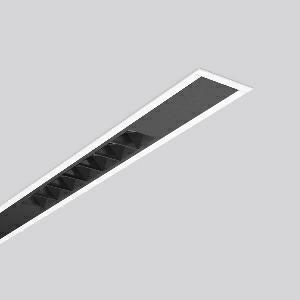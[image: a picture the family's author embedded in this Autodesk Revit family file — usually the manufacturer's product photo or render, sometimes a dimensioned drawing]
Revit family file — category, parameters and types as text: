
# Revit family: less_is_more_beamline_312481_002_1_76_a936
name_source: partatom
category: Lighting Fixtures
units: mm (PartAtom-declared; Revit-internal decimal feet)

## family parameters
Cut with Voids When Loaded = No
Host = Face
Light Source = No
Part Type = Normal
Room Calculation Point = No
Round Connector Dimension = Use Diameter
Shared = No

## types (1)
- LESS IS MORE BEAMLINE (1 x LED Modul 940, 1887.5 lm, 4000)
    Apparent Load = 97 VA
    CIE Flux Codes = 100 100 100 100 100
    Color Rendering = 92
    Color Temperature = 4000
    Default Elevation = 1800 mm
    Description = Series: LESS IS MORE BEAMLINE
Linear recessed ceiling and wall luminaire for aesthetically sophisticated lighting. Luminaire with four LED light units. Housing: extruded aluminium profile, powder-coated. End cap aluminium powder-coated. LED light unit with MRS technology: Mini-Reflector-System made of metallised thermoplastic with prismatic black glare-suppressing frame for pleasant glare-free light (RUG < 10). Each LED light unit has 7 reflector elements. Medium beam light distribution. Ceiling installation with pre-assembled SBS mounting system. LED unit with integrated converter interchangeable and removable. Suitable for through-wiring. 
Colour: traffic white, matt (RAL 9016)
Length: 2262 mm
Width: 71 mm
Height: 1.5 mm
Cut-out length: 2243 mm
Cut-out width: 60 mm
Recess height: 125 mm
Luminaire: recess height: 106 mm
Lamp: LED
Socket: without socket
Colour temperature: 4000K
Colour rendering index (CRI): 90
System power: 97 W
Rated luminous flux: 7550 lm
Luminous efficiency: 78 lm/W
Control gear: Converter, dimmable, DALI
Protection class: I
Type of protection: IP 20
    Height = 0 mm  [stored 0 ft]
    Lamp = 1 x LED Modul 940
    Lamp Light Flux = 1887.5 lm
    Lamp count = 1
    Length = 2262 mm
    Lifetime = 50000 h
    Luminous efficacy = 78 lm/W
    Manufacturer = RZB
    ModVariant = No
    Model = 312481.002.1.76
    Mounting Place = Ceiling, Wall
    Mounting Type = Recessed
    Number of Poles = 1
    OnlyDefault = Yes
    Power Factor = 1
    Product Name = LESS IS MORE BEAMLINE
    Product group = Recessed LED linear luminaires
    ProductGroupID = 407
    Protection Class = Protection class I
    Protection Degree = IP 20
    RLX_Detail_Level = 1
    RLX_Emergency_Light_Flux = 0 lm
    RLX_Emergency_Type = 0
    RLX_Emergency_Type_DB = No
    RlxData = <blob elided: 24325 chars, md5=9b457ee7>
    Socket = socket
    Standby Power = 0 W
    System Light Flux = 7550 lm
    System Power = 97 W
    Type Comments = Product without accessories
    Type Image = 312465.002.jpg
    URL = http://relux.com
    VarID = ---
    Voltage = 230 V
    Voltage Range = 220-240 V
    Weight = 0.00 kg
    Width = 71 mm

note: [stored X ft] marks values corroborated as IEEE doubles in the binary element streams (Revit-internal decimal feet)

## geometry (parser evidence)
native form markers: Blend x4, Sweep x19
no freeform markers — native parametric forms only
